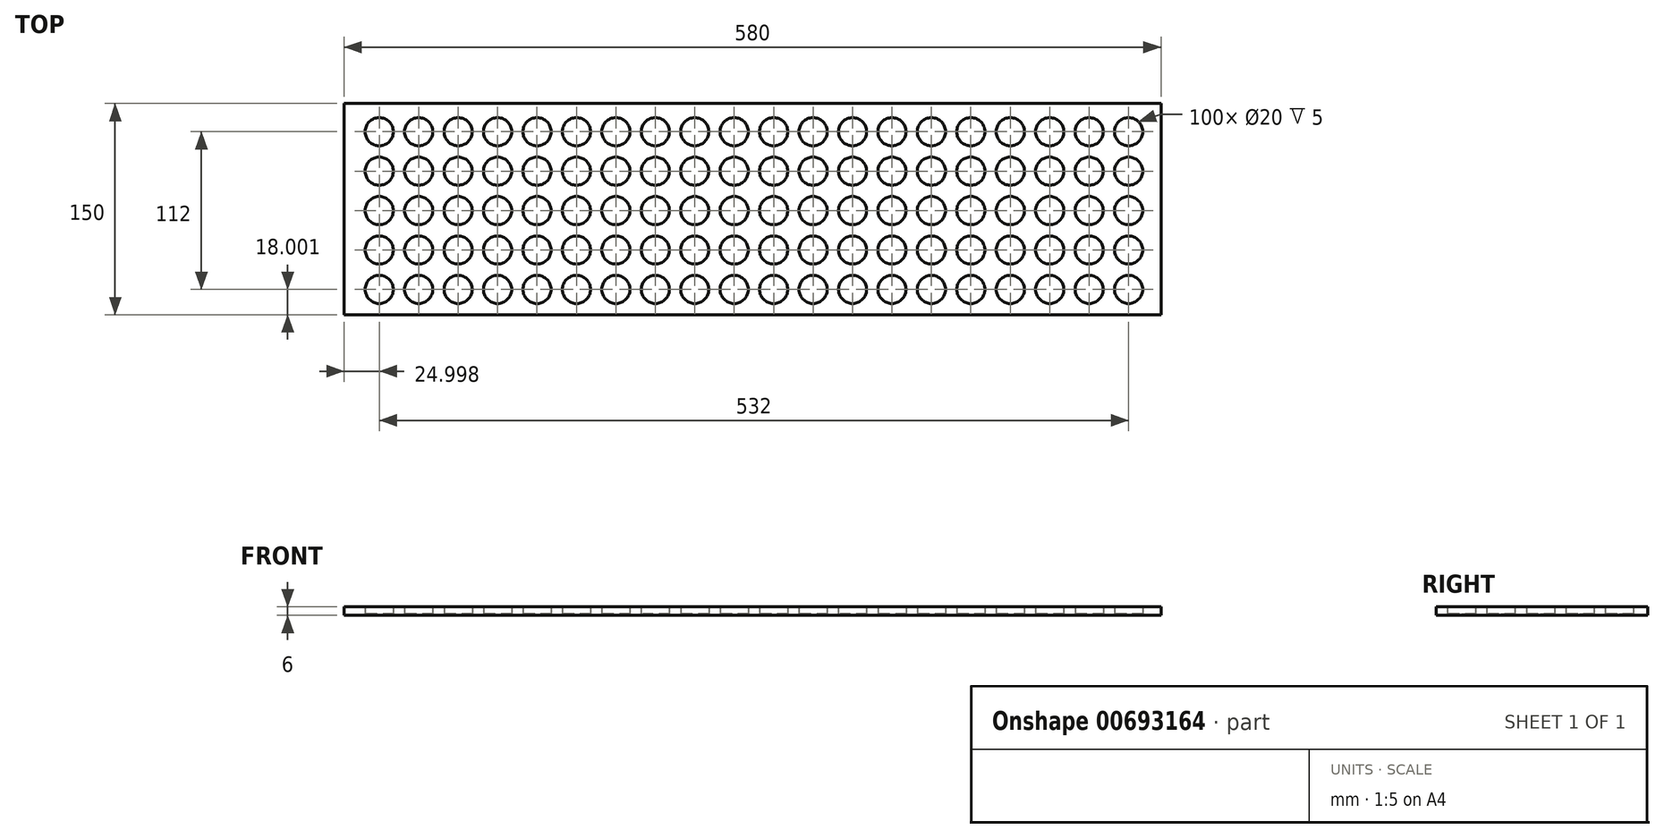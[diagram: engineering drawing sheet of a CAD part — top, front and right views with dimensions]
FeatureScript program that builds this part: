
annotation { "Feature Type Name" : "Feature", "Feature Type Description" : "" }
export const myFeature = defineFeature(function(context is Context, id is Id, definition is map)
    precondition{}
    {
        {
            var Q0;
            Q0=qCreatedBy(makeId("Top.planeOp"),FACE);
            var sketch = newSketch(context, id + "F0", { "sketchPlane" : qUnion([Q0])});
            skLineSegment(sketch, "E0.bottom", {"start": v(-288.8, 31.74) * mm, "end": v(291.2, 31.74) * mm});
            skLineSegment(sketch, "E0.top", {"start": v(-288.8, -118.26) * mm, "end": v(291.2, -118.26) * mm});
            skLineSegment(sketch, "E0.left", {"start": v(-288.8, 31.74) * mm, "end": v(-288.8, -118.26) * mm});
            skLineSegment(sketch, "E0.right", {"start": v(291.2, 31.74) * mm, "end": v(291.2, -118.26) * mm});
            skCircle(sketch, "E1", {"center": v(-263.8, 11.74) * mm, "radius": 10 * mm});
            skCircle(sketch, "E2.0.1.0", {"center": v(-263.8, -16.26) * mm, "radius": 10 * mm});
            skCircle(sketch, "E2.0.2.0", {"center": v(-263.8, -44.26) * mm, "radius": 10 * mm});
            skCircle(sketch, "E2.0.3.0", {"center": v(-263.8, -72.26) * mm, "radius": 10 * mm});
            skCircle(sketch, "E2.0.4.0", {"center": v(-263.8, -100.26) * mm, "radius": 10 * mm});
            skCircle(sketch, "E2.1.0.0", {"center": v(-235.8, 11.74) * mm, "radius": 10 * mm});
            skCircle(sketch, "E2.1.1.0", {"center": v(-235.8, -16.26) * mm, "radius": 10 * mm});
            skCircle(sketch, "E2.1.2.0", {"center": v(-235.8, -44.26) * mm, "radius": 10 * mm});
            skCircle(sketch, "E2.1.3.0", {"center": v(-235.8, -72.26) * mm, "radius": 10 * mm});
            skCircle(sketch, "E2.1.4.0", {"center": v(-235.8, -100.26) * mm, "radius": 10 * mm});
            skCircle(sketch, "E2.2.0.0", {"center": v(-207.8, 11.74) * mm, "radius": 10 * mm});
            skCircle(sketch, "E2.2.1.0", {"center": v(-207.8, -16.26) * mm, "radius": 10 * mm});
            skCircle(sketch, "E2.2.2.0", {"center": v(-207.8, -44.26) * mm, "radius": 10 * mm});
            skCircle(sketch, "E2.2.3.0", {"center": v(-207.8, -72.26) * mm, "radius": 10 * mm});
            skCircle(sketch, "E2.2.4.0", {"center": v(-207.8, -100.26) * mm, "radius": 10 * mm});
            skCircle(sketch, "E2.3.0.0", {"center": v(-179.8, 11.74) * mm, "radius": 10 * mm});
            skCircle(sketch, "E2.3.1.0", {"center": v(-179.8, -16.26) * mm, "radius": 10 * mm});
            skCircle(sketch, "E2.3.2.0", {"center": v(-179.8, -44.26) * mm, "radius": 10 * mm});
            skCircle(sketch, "E2.3.3.0", {"center": v(-179.8, -72.26) * mm, "radius": 10 * mm});
            skCircle(sketch, "E2.3.4.0", {"center": v(-179.8, -100.26) * mm, "radius": 10 * mm});
            skCircle(sketch, "E2.4.0.0", {"center": v(-151.8, 11.74) * mm, "radius": 10 * mm});
            skCircle(sketch, "E2.4.1.0", {"center": v(-151.8, -16.26) * mm, "radius": 10 * mm});
            skCircle(sketch, "E2.4.2.0", {"center": v(-151.8, -44.26) * mm, "radius": 10 * mm});
            skCircle(sketch, "E2.4.3.0", {"center": v(-151.8, -72.26) * mm, "radius": 10 * mm});
            skCircle(sketch, "E2.4.4.0", {"center": v(-151.8, -100.26) * mm, "radius": 10 * mm});
            skCircle(sketch, "E2.5.0.0", {"center": v(-123.8, 11.74) * mm, "radius": 10 * mm});
            skCircle(sketch, "E2.5.1.0", {"center": v(-123.8, -16.26) * mm, "radius": 10 * mm});
            skCircle(sketch, "E2.5.2.0", {"center": v(-123.8, -44.26) * mm, "radius": 10 * mm});
            skCircle(sketch, "E2.5.3.0", {"center": v(-123.8, -72.26) * mm, "radius": 10 * mm});
            skCircle(sketch, "E2.5.4.0", {"center": v(-123.8, -100.26) * mm, "radius": 10 * mm});
            skCircle(sketch, "E2.6.0.0", {"center": v(-95.8, 11.74) * mm, "radius": 10 * mm});
            skCircle(sketch, "E2.6.1.0", {"center": v(-95.8, -16.26) * mm, "radius": 10 * mm});
            skCircle(sketch, "E2.6.2.0", {"center": v(-95.8, -44.26) * mm, "radius": 10 * mm});
            skCircle(sketch, "E2.6.3.0", {"center": v(-95.8, -72.26) * mm, "radius": 10 * mm});
            skCircle(sketch, "E2.6.4.0", {"center": v(-95.8, -100.26) * mm, "radius": 10 * mm});
            skCircle(sketch, "E2.7.0.0", {"center": v(-67.8, 11.74) * mm, "radius": 10 * mm});
            skCircle(sketch, "E2.7.1.0", {"center": v(-67.8, -16.26) * mm, "radius": 10 * mm});
            skCircle(sketch, "E2.7.2.0", {"center": v(-67.8, -44.26) * mm, "radius": 10 * mm});
            skCircle(sketch, "E2.7.3.0", {"center": v(-67.8, -72.26) * mm, "radius": 10 * mm});
            skCircle(sketch, "E2.7.4.0", {"center": v(-67.8, -100.26) * mm, "radius": 10 * mm});
            skCircle(sketch, "E2.8.0.0", {"center": v(-39.8, 11.74) * mm, "radius": 10 * mm});
            skCircle(sketch, "E2.8.1.0", {"center": v(-39.8, -16.26) * mm, "radius": 10 * mm});
            skCircle(sketch, "E2.8.2.0", {"center": v(-39.8, -44.26) * mm, "radius": 10 * mm});
            skCircle(sketch, "E2.8.3.0", {"center": v(-39.8, -72.26) * mm, "radius": 10 * mm});
            skCircle(sketch, "E2.8.4.0", {"center": v(-39.8, -100.26) * mm, "radius": 10 * mm});
            skCircle(sketch, "E2.9.0.0", {"center": v(-11.8, 11.74) * mm, "radius": 10 * mm});
            skCircle(sketch, "E2.9.1.0", {"center": v(-11.8, -16.26) * mm, "radius": 10 * mm});
            skCircle(sketch, "E2.9.2.0", {"center": v(-11.8, -44.26) * mm, "radius": 10 * mm});
            skCircle(sketch, "E2.9.3.0", {"center": v(-11.8, -72.26) * mm, "radius": 10 * mm});
            skCircle(sketch, "E2.9.4.0", {"center": v(-11.8, -100.26) * mm, "radius": 10 * mm});
            skCircle(sketch, "E2.10.0.0", {"center": v(16.2, 11.74) * mm, "radius": 10 * mm});
            skCircle(sketch, "E2.10.1.0", {"center": v(16.2, -16.26) * mm, "radius": 10 * mm});
            skCircle(sketch, "E2.10.2.0", {"center": v(16.2, -44.26) * mm, "radius": 10 * mm});
            skCircle(sketch, "E2.10.3.0", {"center": v(16.2, -72.26) * mm, "radius": 10 * mm});
            skCircle(sketch, "E2.10.4.0", {"center": v(16.2, -100.26) * mm, "radius": 10 * mm});
            skCircle(sketch, "E2.11.0.0", {"center": v(44.2, 11.74) * mm, "radius": 10 * mm});
            skCircle(sketch, "E2.11.1.0", {"center": v(44.2, -16.26) * mm, "radius": 10 * mm});
            skCircle(sketch, "E2.11.2.0", {"center": v(44.2, -44.26) * mm, "radius": 10 * mm});
            skCircle(sketch, "E2.11.3.0", {"center": v(44.2, -72.26) * mm, "radius": 10 * mm});
            skCircle(sketch, "E2.11.4.0", {"center": v(44.2, -100.26) * mm, "radius": 10 * mm});
            skCircle(sketch, "E2.12.0.0", {"center": v(72.2, 11.74) * mm, "radius": 10 * mm});
            skCircle(sketch, "E2.12.1.0", {"center": v(72.2, -16.26) * mm, "radius": 10 * mm});
            skCircle(sketch, "E2.12.2.0", {"center": v(72.2, -44.26) * mm, "radius": 10 * mm});
            skCircle(sketch, "E2.12.3.0", {"center": v(72.2, -72.26) * mm, "radius": 10 * mm});
            skCircle(sketch, "E2.12.4.0", {"center": v(72.2, -100.26) * mm, "radius": 10 * mm});
            skCircle(sketch, "E2.13.0.0", {"center": v(100.2, 11.74) * mm, "radius": 10 * mm});
            skCircle(sketch, "E2.13.1.0", {"center": v(100.2, -16.26) * mm, "radius": 10 * mm});
            skCircle(sketch, "E2.13.2.0", {"center": v(100.2, -44.26) * mm, "radius": 10 * mm});
            skCircle(sketch, "E2.13.3.0", {"center": v(100.2, -72.26) * mm, "radius": 10 * mm});
            skCircle(sketch, "E2.13.4.0", {"center": v(100.2, -100.26) * mm, "radius": 10 * mm});
            skCircle(sketch, "E2.14.0.0", {"center": v(128.2, 11.74) * mm, "radius": 10 * mm});
            skCircle(sketch, "E2.14.1.0", {"center": v(128.2, -16.26) * mm, "radius": 10 * mm});
            skCircle(sketch, "E2.14.2.0", {"center": v(128.2, -44.26) * mm, "radius": 10 * mm});
            skCircle(sketch, "E2.14.3.0", {"center": v(128.2, -72.26) * mm, "radius": 10 * mm});
            skCircle(sketch, "E2.14.4.0", {"center": v(128.2, -100.26) * mm, "radius": 10 * mm});
            skCircle(sketch, "E2.15.0.0", {"center": v(156.2, 11.74) * mm, "radius": 10 * mm});
            skCircle(sketch, "E2.15.1.0", {"center": v(156.2, -16.26) * mm, "radius": 10 * mm});
            skCircle(sketch, "E2.15.2.0", {"center": v(156.2, -44.26) * mm, "radius": 10 * mm});
            skCircle(sketch, "E2.15.3.0", {"center": v(156.2, -72.26) * mm, "radius": 10 * mm});
            skCircle(sketch, "E2.15.4.0", {"center": v(156.2, -100.26) * mm, "radius": 10 * mm});
            skCircle(sketch, "E2.16.0.0", {"center": v(184.2, 11.74) * mm, "radius": 10 * mm});
            skCircle(sketch, "E2.16.1.0", {"center": v(184.2, -16.26) * mm, "radius": 10 * mm});
            skCircle(sketch, "E2.16.2.0", {"center": v(184.2, -44.26) * mm, "radius": 10 * mm});
            skCircle(sketch, "E2.16.3.0", {"center": v(184.2, -72.26) * mm, "radius": 10 * mm});
            skCircle(sketch, "E2.16.4.0", {"center": v(184.2, -100.26) * mm, "radius": 10 * mm});
            skCircle(sketch, "E2.17.0.0", {"center": v(212.2, 11.74) * mm, "radius": 10 * mm});
            skCircle(sketch, "E2.17.1.0", {"center": v(212.2, -16.26) * mm, "radius": 10 * mm});
            skCircle(sketch, "E2.17.2.0", {"center": v(212.2, -44.26) * mm, "radius": 10 * mm});
            skCircle(sketch, "E2.17.3.0", {"center": v(212.2, -72.26) * mm, "radius": 10 * mm});
            skCircle(sketch, "E2.17.4.0", {"center": v(212.2, -100.26) * mm, "radius": 10 * mm});
            skCircle(sketch, "E2.18.0.0", {"center": v(240.2, 11.74) * mm, "radius": 10 * mm});
            skCircle(sketch, "E2.18.1.0", {"center": v(240.2, -16.26) * mm, "radius": 10 * mm});
            skCircle(sketch, "E2.18.2.0", {"center": v(240.2, -44.26) * mm, "radius": 10 * mm});
            skCircle(sketch, "E2.18.3.0", {"center": v(240.2, -72.26) * mm, "radius": 10 * mm});
            skCircle(sketch, "E2.18.4.0", {"center": v(240.2, -100.26) * mm, "radius": 10 * mm});
            skCircle(sketch, "E2.19.0.0", {"center": v(268.2, 11.74) * mm, "radius": 10 * mm});
            skCircle(sketch, "E2.19.1.0", {"center": v(268.2, -16.26) * mm, "radius": 10 * mm});
            skCircle(sketch, "E2.19.2.0", {"center": v(268.2, -44.26) * mm, "radius": 10 * mm});
            skCircle(sketch, "E2.19.3.0", {"center": v(268.2, -72.26) * mm, "radius": 10 * mm});
            skCircle(sketch, "E2.19.4.0", {"center": v(268.2, -100.26) * mm, "radius": 10 * mm});
            skLineSegment(sketch, "E2.direction1", {"start": v(-263.8, 6.74) * mm, "end": v(-235.8, 6.74) * mm, "construction": true});
            skLineSegment(sketch, "E2.direction2", {"start": v(-263.8, 6.74) * mm, "end": v(-263.8, -21.26) * mm, "construction": true});
            skSolve(sketch);
        }
        {
            var Q0;
            Q0=qSketchRegion(id+"F0",true);
            extrude(context, id + "F1", {"entities" : qUnion([Q0]), "depth" : 5 * mm, "offsetDistance" : 25 * mm});
        }
        {
            var Q0;
            Q0=makeQuery(id+"F1.opExtrude","CAP_FACE",FACE,{"disambiguationData":[OSD([sQuery(id+"F0.wireOp",EDGE,"E0.bottom"),sQuery(id+"F0.wireOp",EDGE,"E0.top"),sQuery(id+"F0.wireOp",EDGE,"E0.left"),sQuery(id+"F0.wireOp",EDGE,"E0.right"),sQuery(id+"F0.wireOp",EDGE,"Q3saARHD-Gs58-2NVK-PtzY-fhxvJSEAU8xS.bottom"),sQuery(id+"F0.wireOp",EDGE,"Q3saARHD-Gs58-2NVK-PtzY-fhxvJSEAU8xS.top"),sQuery(id+"F0.wireOp",EDGE,"Q3saARHD-Gs58-2NVK-PtzY-fhxvJSEAU8xS.left"),sQuery(id+"F0.wireOp",EDGE,"Q3saARHD-Gs58-2NVK-PtzY-fhxvJSEAU8xS.right"),sQuery(id+"F0.wireOp",EDGE,"dcdc5563-4537-49a2-8787-ece9258b1a45.0.1.0"),sQuery(id+"F0.wireOp",EDGE,"dcdc5563-4537-49a2-8787-ece9258b1a45.0.1.1"),sQuery(id+"F0.wireOp",EDGE,"dcdc5563-4537-49a2-8787-ece9258b1a45.0.1.2"),sQuery(id+"F0.wireOp",EDGE,"dcdc5563-4537-49a2-8787-ece9258b1a45.0.1.3"),sQuery(id+"F0.wireOp",EDGE,"dcdc5563-4537-49a2-8787-ece9258b1a45.0.2.0"),sQuery(id+"F0.wireOp",EDGE,"dcdc5563-4537-49a2-8787-ece9258b1a45.0.2.1"),sQuery(id+"F0.wireOp",EDGE,"dcdc5563-4537-49a2-8787-ece9258b1a45.0.2.2"),sQuery(id+"F0.wireOp",EDGE,"dcdc5563-4537-49a2-8787-ece9258b1a45.0.2.3"),sQuery(id+"F0.wireOp",EDGE,"dcdc5563-4537-49a2-8787-ece9258b1a45.0.3.0"),sQuery(id+"F0.wireOp",EDGE,"dcdc5563-4537-49a2-8787-ece9258b1a45.0.3.1"),sQuery(id+"F0.wireOp",EDGE,"dcdc5563-4537-49a2-8787-ece9258b1a45.0.3.2"),sQuery(id+"F0.wireOp",EDGE,"dcdc5563-4537-49a2-8787-ece9258b1a45.0.3.3"),sQuery(id+"F0.wireOp",EDGE,"dcdc5563-4537-49a2-8787-ece9258b1a45.0.4.0"),sQuery(id+"F0.wireOp",EDGE,"dcdc5563-4537-49a2-8787-ece9258b1a45.0.4.1"),sQuery(id+"F0.wireOp",EDGE,"dcdc5563-4537-49a2-8787-ece9258b1a45.0.4.2"),sQuery(id+"F0.wireOp",EDGE,"dcdc5563-4537-49a2-8787-ece9258b1a45.0.4.3"),sQuery(id+"F0.wireOp",EDGE,"dcdc5563-4537-49a2-8787-ece9258b1a45.0.5.0"),sQuery(id+"F0.wireOp",EDGE,"dcdc5563-4537-49a2-8787-ece9258b1a45.0.5.1"),sQuery(id+"F0.wireOp",EDGE,"dcdc5563-4537-49a2-8787-ece9258b1a45.0.5.2"),sQuery(id+"F0.wireOp",EDGE,"dcdc5563-4537-49a2-8787-ece9258b1a45.0.5.3"),sQuery(id+"F0.wireOp",EDGE,"dcdc5563-4537-49a2-8787-ece9258b1a45.0.6.0"),sQuery(id+"F0.wireOp",EDGE,"dcdc5563-4537-49a2-8787-ece9258b1a45.0.6.1"),sQuery(id+"F0.wireOp",EDGE,"dcdc5563-4537-49a2-8787-ece9258b1a45.0.6.2"),sQuery(id+"F0.wireOp",EDGE,"dcdc5563-4537-49a2-8787-ece9258b1a45.0.6.3")])],"isStart":true});
            var sketch = newSketch(context, id + "F2", { "sketchPlane" : qUnion([Q0])});
            skLineSegment(sketch, "E3.bottom", {"start": v(-288.8, -31.74) * mm, "end": v(291.2, -31.74) * mm});
            skLineSegment(sketch, "E3.top", {"start": v(-288.8, 118.26) * mm, "end": v(291.2, 118.26) * mm});
            skLineSegment(sketch, "E3.left", {"start": v(-288.8, -31.74) * mm, "end": v(-288.8, 118.26) * mm});
            skLineSegment(sketch, "E3.right", {"start": v(291.2, -31.74) * mm, "end": v(291.2, 118.26) * mm});
            skSolve(sketch);
        }
        {
            var Q0;
            Q0=qSketchRegion(id+"F2",true);
            extrude(context, id + "F3", {"entities" : qUnion([Q0]), "operationType" : NewBodyOperationType.ADD, "depth" : 1 * mm, "offsetDistance" : 25 * mm});
        }
    });
